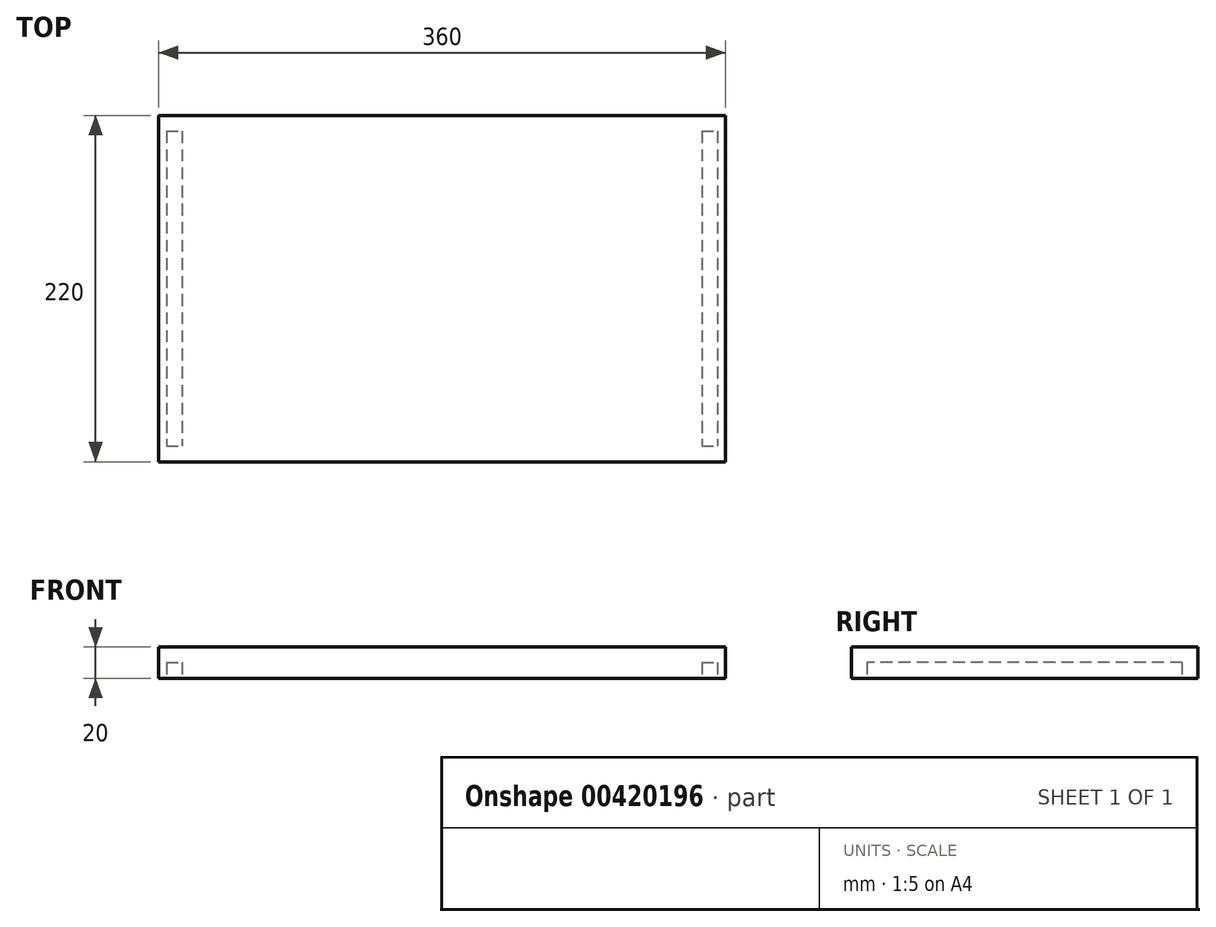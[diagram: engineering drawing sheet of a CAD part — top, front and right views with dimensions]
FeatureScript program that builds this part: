
annotation { "Feature Type Name" : "Feature", "Feature Type Description" : "" }
export const myFeature = defineFeature(function(context is Context, id is Id, definition is map)
    precondition{}
    {
        {
            var Q0;
            Q0=qCreatedBy(makeId("Top.planeOp"),FACE);
            var sketch = newSketch(context, id + "F0", { "sketchPlane" : qUnion([Q0])});
            skLineSegment(sketch, "E0.bottom", {"start": v(-180, 110) * mm, "end": v(180, 110) * mm});
            skLineSegment(sketch, "E0.top", {"start": v(-180, -110) * mm, "end": v(180, -110) * mm});
            skLineSegment(sketch, "E0.left", {"start": v(-180, 110) * mm, "end": v(-180, -110) * mm});
            skLineSegment(sketch, "E0.right", {"start": v(180, 110) * mm, "end": v(180, -110) * mm});
            skPoint(sketch, "E0.middle", {"position": v(0, 0) * mm});
            skSolve(sketch);
        }
        {
            var Q0;
            Q0 = qSketchRegion(id + "F0", true);
            extrude(context, id + "F1", {"entities" : qUnion([Q0]), "depth" : 20 * mm});
        }
        {
            var Q0;
            Q0=qCreatedBy(makeId("Top.planeOp"),FACE);
            var sketch = newSketch(context, id + "F2", { "sketchPlane" : qUnion([Q0])});
            skLineSegment(sketch, "E1.bottom", {"start": v(-175, 100) * mm, "end": v(-165, 100) * mm});
            skLineSegment(sketch, "E1.top", {"start": v(-175, -100) * mm, "end": v(-165, -100) * mm});
            skLineSegment(sketch, "E1.left", {"start": v(-175, 100) * mm, "end": v(-175, -100) * mm});
            skLineSegment(sketch, "E1.right", {"start": v(-165, 100) * mm, "end": v(-165, -100) * mm});
            skSolve(sketch);
        }
        {
            var Q0;
            Q0 = qSketchRegion(id + "F2", true);
            extrude(context, id + "F3", {"entities" : qUnion([Q0]), "operationType" : NewBodyOperationType.REMOVE, "depth" : 10 * mm});
        }
        {
            var Q0;
            Q0=qCreatedBy(makeId("Top.planeOp"),FACE);
            var sketch = newSketch(context, id + "F4", { "sketchPlane" : qUnion([Q0])});
            skLineSegment(sketch, "E2.bottom", {"start": v(165, 100) * mm, "end": v(175, 100) * mm});
            skLineSegment(sketch, "E2.top", {"start": v(165, -100) * mm, "end": v(175, -100) * mm});
            skLineSegment(sketch, "E2.left", {"start": v(165, 100) * mm, "end": v(165, -100) * mm});
            skLineSegment(sketch, "E2.right", {"start": v(175, 100) * mm, "end": v(175, -100) * mm});
            skSolve(sketch);
        }
        {
            var Q0;
            Q0 = qSketchRegion(id + "F4", true);
            extrude(context, id + "F5", {"entities" : qUnion([Q0]), "operationType" : NewBodyOperationType.REMOVE, "depth" : 10 * mm});
        }
    });
